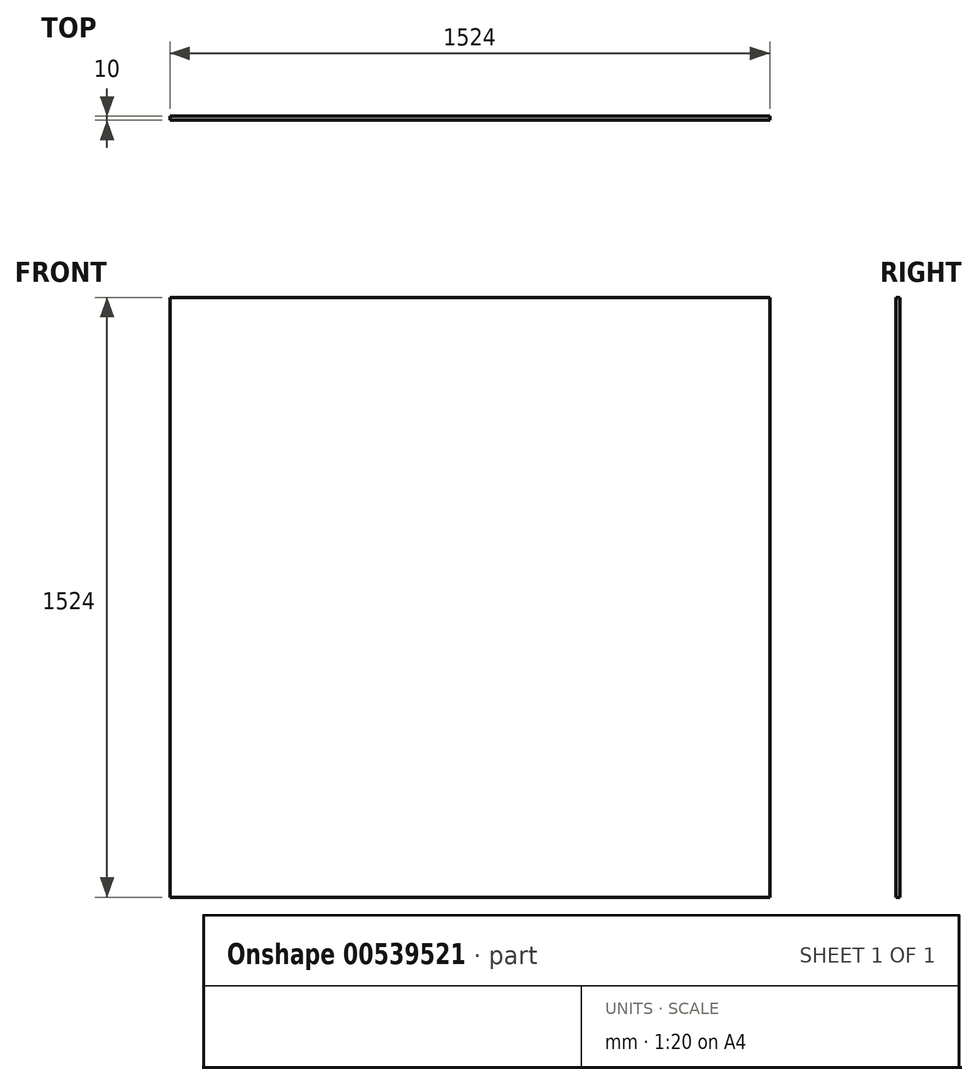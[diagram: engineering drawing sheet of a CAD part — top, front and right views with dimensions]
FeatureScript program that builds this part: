
annotation { "Feature Type Name" : "Feature", "Feature Type Description" : "" }
export const myFeature = defineFeature(function(context is Context, id is Id, definition is map)
    precondition{}
    {
        {
            var Q0;
            Q0=qCreatedBy(makeId("Front.planeOp"),FACE);
            var sketch = newSketch(context, id + "F0", { "sketchPlane" : qUnion([Q0])});
            skLineSegment(sketch, "E0.bottom", {"start": v(762, -762) * mm, "end": v(-762, -762) * mm});
            skLineSegment(sketch, "E0.top", {"start": v(762, 762) * mm, "end": v(-762, 762) * mm});
            skLineSegment(sketch, "E0.left", {"start": v(762, -762) * mm, "end": v(762, 762) * mm});
            skLineSegment(sketch, "E0.right", {"start": v(-762, -762) * mm, "end": v(-762, 762) * mm});
            skPoint(sketch, "E0.middle", {"position": v(0, 0) * mm});
            skSolve(sketch);
        }
        {
            var Q0;
            Q0=makeQuery(id+"F0.imprint","IMPRINT",FACE,{"disambiguationData":[TD([[makeQuery(id+"F0.imprint","IMPRINT",EDGE,{"derivedFrom":sQuery(id+"F0.wireOp",EDGE,"E0.bottom")}),-1.0]])]});
            extrude(context, id + "F1", {"entities" : qUnion([Q0]), "depth" : 10 * mm});
        }
    });
